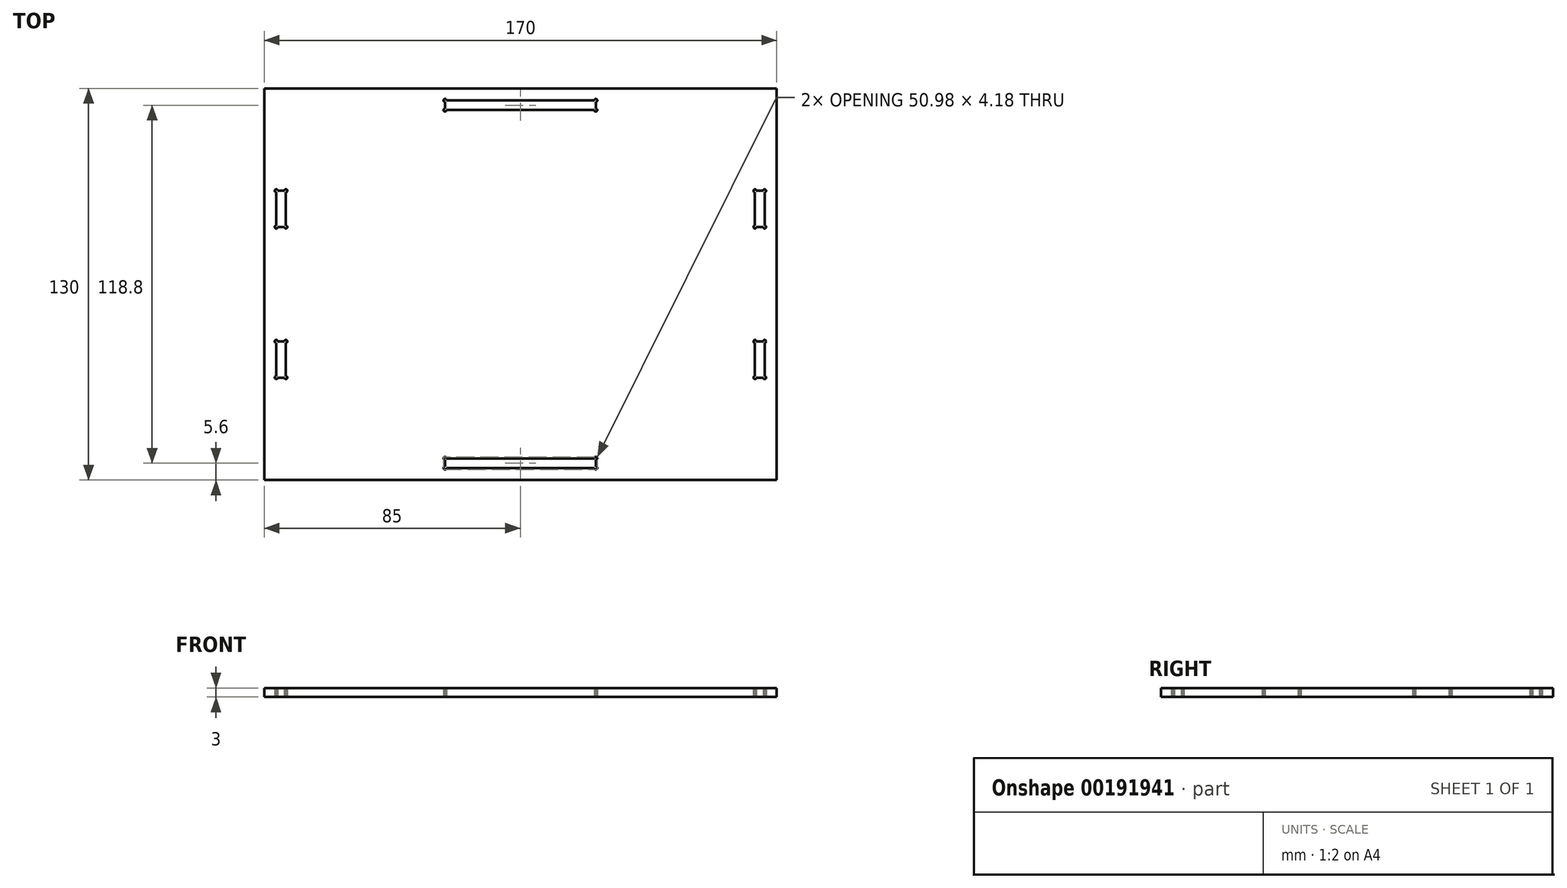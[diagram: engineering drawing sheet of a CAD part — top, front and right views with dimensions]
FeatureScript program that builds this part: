
annotation { "Feature Type Name" : "Feature", "Feature Type Description" : "" }
export const myFeature = defineFeature(function(context is Context, id is Id, definition is map)
    precondition{}
    {
        {
            var Q0;
            Q0=qCreatedBy(makeId("Top.planeOp"),FACE);
            var sketch = newSketch(context, id + "F0", { "sketchPlane" : qUnion([Q0])});
            skLineSegment(sketch, "E0.bottom", {"start": v(85, -65) * mm, "end": v(-85, -65) * mm});
            skLineSegment(sketch, "E0.top", {"start": v(85, 65) * mm, "end": v(-85, 65) * mm});
            skLineSegment(sketch, "E0.left", {"start": v(85, -65) * mm, "end": v(85, 65) * mm});
            skLineSegment(sketch, "E0.right", {"start": v(-85, -65) * mm, "end": v(-85, 65) * mm});
            skPoint(sketch, "E0.middle", {"position": v(0, 0) * mm});
            skLineSegment(sketch, "E1.bottom", {"start": v(-25, -57.8) * mm, "end": v(25, -57.8) * mm});
            skLineSegment(sketch, "E1.top", {"start": v(-25, -61) * mm, "end": v(25, -61) * mm});
            skLineSegment(sketch, "E1.left", {"start": v(-25, -57.8) * mm, "end": v(-25, -61) * mm});
            skLineSegment(sketch, "E1.right", {"start": v(25, -57.8) * mm, "end": v(25, -61) * mm});
            skCircle(sketch, "E2", {"center": v(-25, -57.8) * mm, "radius": 0.5 * mm});
            skCircle(sketch, "E3", {"center": v(-25, -61) * mm, "radius": 0.5 * mm});
            skCircle(sketch, "E4", {"center": v(25, -57.8) * mm, "radius": 0.5 * mm});
            skCircle(sketch, "E5", {"center": v(25, -61) * mm, "radius": 0.5 * mm});
            skCircle(sketch, "E6.MirrorC", {"center": v(-25, 61) * mm, "radius": 0.5 * mm});
            skCircle(sketch, "E7.MirrorC", {"center": v(-25, 57.8) * mm, "radius": 0.5 * mm});
            skLineSegment(sketch, "E8.MirrorCS", {"start": v(25, 57.8) * mm, "end": v(25, 61) * mm});
            skLineSegment(sketch, "E9.MirrorCS", {"start": v(-25, 57.8) * mm, "end": v(-25, 61) * mm});
            skCircle(sketch, "E10.MirrorC", {"center": v(25, 61) * mm, "radius": 0.5 * mm});
            skCircle(sketch, "E11.MirrorC", {"center": v(25, 57.8) * mm, "radius": 0.5 * mm});
            skLineSegment(sketch, "E12.MirrorCS", {"start": v(-25, 57.8) * mm, "end": v(25, 57.8) * mm});
            skLineSegment(sketch, "E13.MirrorCS", {"start": v(-25, 61) * mm, "end": v(25, 61) * mm});
            skLineSegment(sketch, "E14.bottom", {"start": v(-81, -19) * mm, "end": v(-77.8, -19) * mm});
            skLineSegment(sketch, "E14.top", {"start": v(-81, -31) * mm, "end": v(-77.8, -31) * mm});
            skLineSegment(sketch, "E14.left", {"start": v(-81, -19) * mm, "end": v(-81, -31) * mm});
            skLineSegment(sketch, "E14.right", {"start": v(-77.8, -19) * mm, "end": v(-77.8, -31) * mm});
            skLineSegment(sketch, "E15.MirrorCS", {"start": v(-81, 19) * mm, "end": v(-81, 31) * mm});
            skLineSegment(sketch, "E16.MirrorCS", {"start": v(-81, 31) * mm, "end": v(-77.8, 31) * mm});
            skLineSegment(sketch, "E17.MirrorCS", {"start": v(-77.8, 19) * mm, "end": v(-77.8, 31) * mm});
            skLineSegment(sketch, "E18.MirrorCS", {"start": v(-81, 19) * mm, "end": v(-77.8, 19) * mm});
            skLineSegment(sketch, "E19.MirrorCS", {"start": v(81, 31) * mm, "end": v(77.8, 31) * mm});
            skLineSegment(sketch, "E20.MirrorCS", {"start": v(81, -19) * mm, "end": v(77.8, -19) * mm});
            skLineSegment(sketch, "E21.MirrorCS", {"start": v(81, 19) * mm, "end": v(77.8, 19) * mm});
            skLineSegment(sketch, "E22.MirrorCS", {"start": v(81, -31) * mm, "end": v(77.8, -31) * mm});
            skLineSegment(sketch, "E23.MirrorCS", {"start": v(81, -19) * mm, "end": v(81, -31) * mm});
            skLineSegment(sketch, "E24.MirrorCS", {"start": v(77.8, 19) * mm, "end": v(77.8, 31) * mm});
            skLineSegment(sketch, "E25.MirrorCS", {"start": v(81, 19) * mm, "end": v(81, 31) * mm});
            skLineSegment(sketch, "E26.MirrorCS", {"start": v(77.8, -19) * mm, "end": v(77.8, -31) * mm});
            skCircle(sketch, "E27", {"center": v(-81, -19) * mm, "radius": 0.5 * mm});
            skCircle(sketch, "E28", {"center": v(-77.8, -19) * mm, "radius": 0.5 * mm});
            skCircle(sketch, "E29", {"center": v(-81, -31) * mm, "radius": 0.5 * mm});
            skCircle(sketch, "E30", {"center": v(-77.8, -31) * mm, "radius": 0.5 * mm});
            skCircle(sketch, "E31.MirrorC", {"center": v(-81, 31) * mm, "radius": 0.5 * mm});
            skCircle(sketch, "E32.MirrorC", {"center": v(-77.8, 31) * mm, "radius": 0.5 * mm});
            skCircle(sketch, "E33.MirrorC", {"center": v(-77.8, 19) * mm, "radius": 0.5 * mm});
            skCircle(sketch, "E34.MirrorC", {"center": v(-81, 19) * mm, "radius": 0.5 * mm});
            skCircle(sketch, "E35.MirrorC", {"center": v(81, -31) * mm, "radius": 0.5 * mm});
            skCircle(sketch, "E36.MirrorC", {"center": v(77.8, -31) * mm, "radius": 0.5 * mm});
            skCircle(sketch, "E37.MirrorC", {"center": v(81, -19) * mm, "radius": 0.5 * mm});
            skCircle(sketch, "E38.MirrorC", {"center": v(77.8, -19) * mm, "radius": 0.5 * mm});
            skCircle(sketch, "E39.MirrorC", {"center": v(81, 31) * mm, "radius": 0.5 * mm});
            skCircle(sketch, "E40.MirrorC", {"center": v(81, 19) * mm, "radius": 0.5 * mm});
            skCircle(sketch, "E41.MirrorC", {"center": v(77.8, 19) * mm, "radius": 0.5 * mm});
            skCircle(sketch, "E42.MirrorC", {"center": v(77.8, 31) * mm, "radius": 0.5 * mm});
            skPoint(sketch, "E43", {"position": v(-77.8, -25) * mm});
            skSolve(sketch);
        }
        {
            var Q0;
            Q0=makeQuery(id+"F0.imprint","IMPRINT",FACE,{"disambiguationData":[TD([[makeQuery(id+"F0.imprint","IMPRINT",EDGE,{"derivedFrom":sQuery(id+"F0.wireOp",EDGE,"E0.bottom")}),-1.0]])]});
            extrude(context, id + "F1", {"entities" : qUnion([Q0]), "depth" : 3 * mm});
        }
    });
